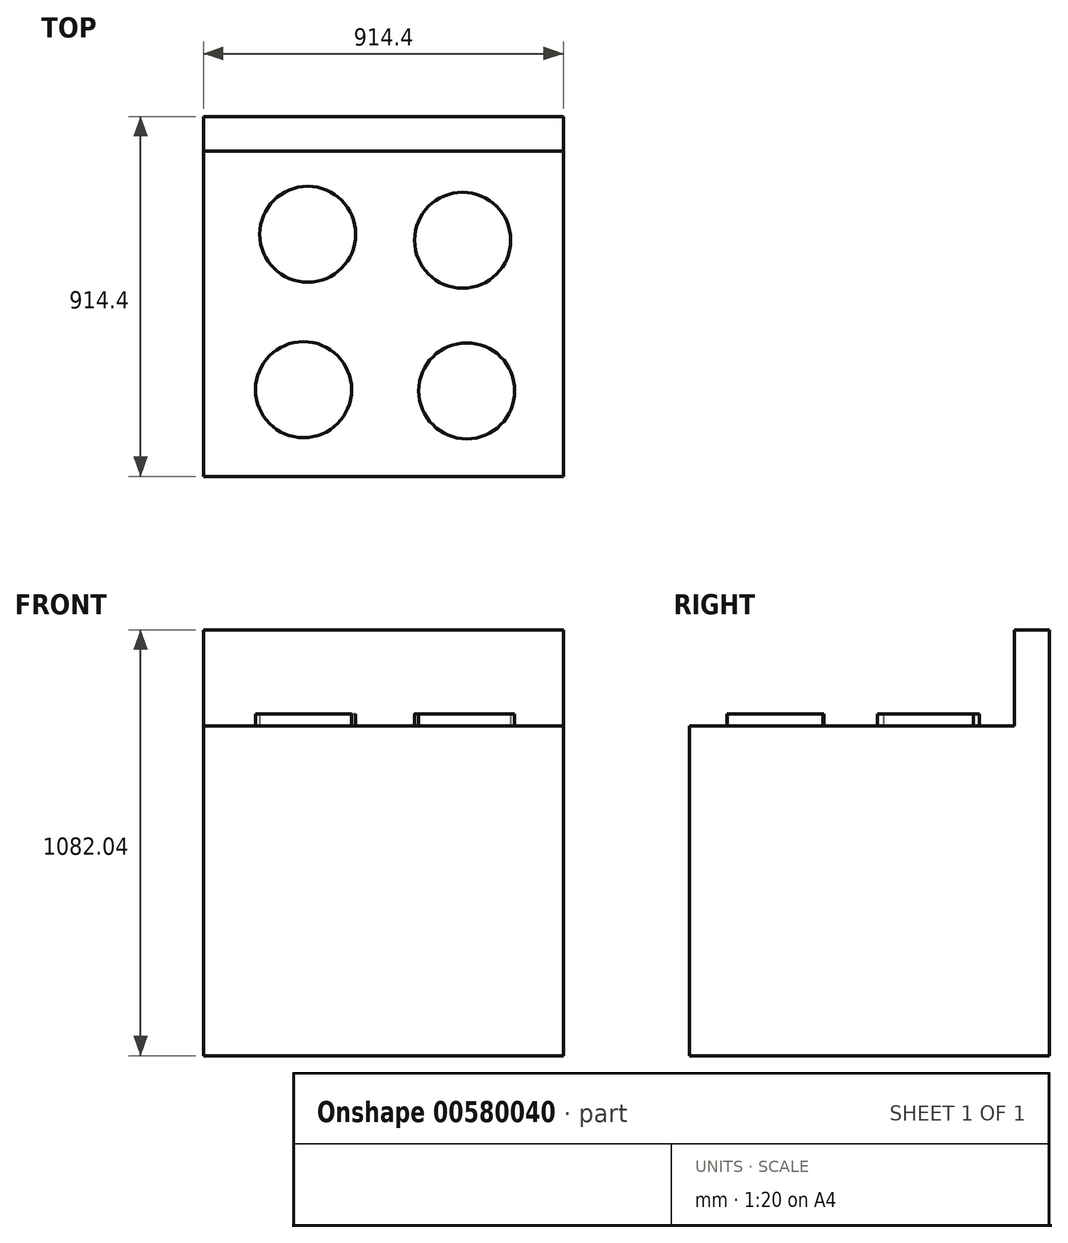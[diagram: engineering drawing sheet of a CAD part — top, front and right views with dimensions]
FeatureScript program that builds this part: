
annotation { "Feature Type Name" : "Feature", "Feature Type Description" : "" }
export const myFeature = defineFeature(function(context is Context, id is Id, definition is map)
    precondition{}
    {
        {
            var Q0;
            Q0=qCreatedBy(makeId("Top.planeOp"),FACE);
            var sketch = newSketch(context, id + "F0", { "sketchPlane" : qUnion([Q0])});
            skLineSegment(sketch, "E0.bottom", {"start": v(-307.74, 670.48) * mm, "end": v(606.66, 670.48) * mm});
            skLineSegment(sketch, "E0.top", {"start": v(-307.74, -243.92) * mm, "end": v(606.66, -243.92) * mm});
            skLineSegment(sketch, "E0.left", {"start": v(-307.74, 670.48) * mm, "end": v(-307.74, -243.92) * mm});
            skLineSegment(sketch, "E0.right", {"start": v(606.66, 670.48) * mm, "end": v(606.66, -243.92) * mm});
            skSolve(sketch);
        }
        {
            var Q0;
            Q0 = qSketchRegion(id + "F0", true);
            extrude(context, id + "F1", {"entities" : qUnion([Q0]), "depth" : 838.2 * mm, "offsetDistance" : 30.48 * mm});
        }
        {
            var Q0;
            Q0=makeQuery(id+"F1.opExtrude","CAP_FACE",FACE,{"disambiguationData":[OSD([sQuery(id+"F0.wireOp",EDGE,"E0.bottom"),sQuery(id+"F0.wireOp",EDGE,"E0.top"),sQuery(id+"F0.wireOp",EDGE,"E0.left"),sQuery(id+"F0.wireOp",EDGE,"E0.right")])],"isStart":false});
            var sketch = newSketch(context, id + "F2", { "sketchPlane" : qUnion([Q0])});
            skCircle(sketch, "E1", {"center": v(350.63, 355.85) * mm, "radius": 121.92 * mm});
            skCircle(sketch, "E2", {"center": v(-42.7, 371.04) * mm, "radius": 121.92 * mm});
            skCircle(sketch, "E3", {"center": v(361.26, -26.85) * mm, "radius": 121.92 * mm});
            skCircle(sketch, "E4", {"center": v(-53.34, -23.82) * mm, "radius": 121.92 * mm});
            skSolve(sketch);
        }
        {
            var Q0;
            Q0 = qSketchRegion(id + "F2", true);
            extrude(context, id + "F3", {"entities" : qUnion([Q0]), "operationType" : NewBodyOperationType.ADD, "depth" : 6.1 * mm, "offsetDistance" : 30.48 * mm});
        }
        {
            var Q0;
            Q0 = qSketchRegion(id + "F2", true);
            extrude(context, id + "F4", {"entities" : qUnion([Q0]), "operationType" : NewBodyOperationType.ADD, "depth" : 30.48 * mm, "offsetDistance" : 30.48 * mm});
        }
        {
            var Q0;
            Q0=makeQuery(id+"F1.opExtrude","CAP_FACE",FACE,{"disambiguationData":[OSD([sQuery(id+"F0.wireOp",EDGE,"E0.bottom"),sQuery(id+"F0.wireOp",EDGE,"E0.top"),sQuery(id+"F0.wireOp",EDGE,"E0.left"),sQuery(id+"F0.wireOp",EDGE,"E0.right")])],"isStart":false});
            var sketch = newSketch(context, id + "F5", { "sketchPlane" : qUnion([Q0])});
            skLineSegment(sketch, "E5.bottom", {"start": v(-307.74, 670.48) * mm, "end": v(606.66, 670.48) * mm});
            skLineSegment(sketch, "E5.top", {"start": v(-307.74, 581.82) * mm, "end": v(606.66, 581.82) * mm});
            skLineSegment(sketch, "E5.left", {"start": v(-307.74, 670.48) * mm, "end": v(-307.74, 581.82) * mm});
            skLineSegment(sketch, "E5.right", {"start": v(606.66, 670.48) * mm, "end": v(606.66, 581.82) * mm});
            skSolve(sketch);
        }
        {
            var Q0;
            Q0 = qSketchRegion(id + "F5", true);
            extrude(context, id + "F6", {"entities" : qUnion([Q0]), "operationType" : NewBodyOperationType.ADD, "depth" : 243.84 * mm, "offsetDistance" : 30.48 * mm});
        }
    });
